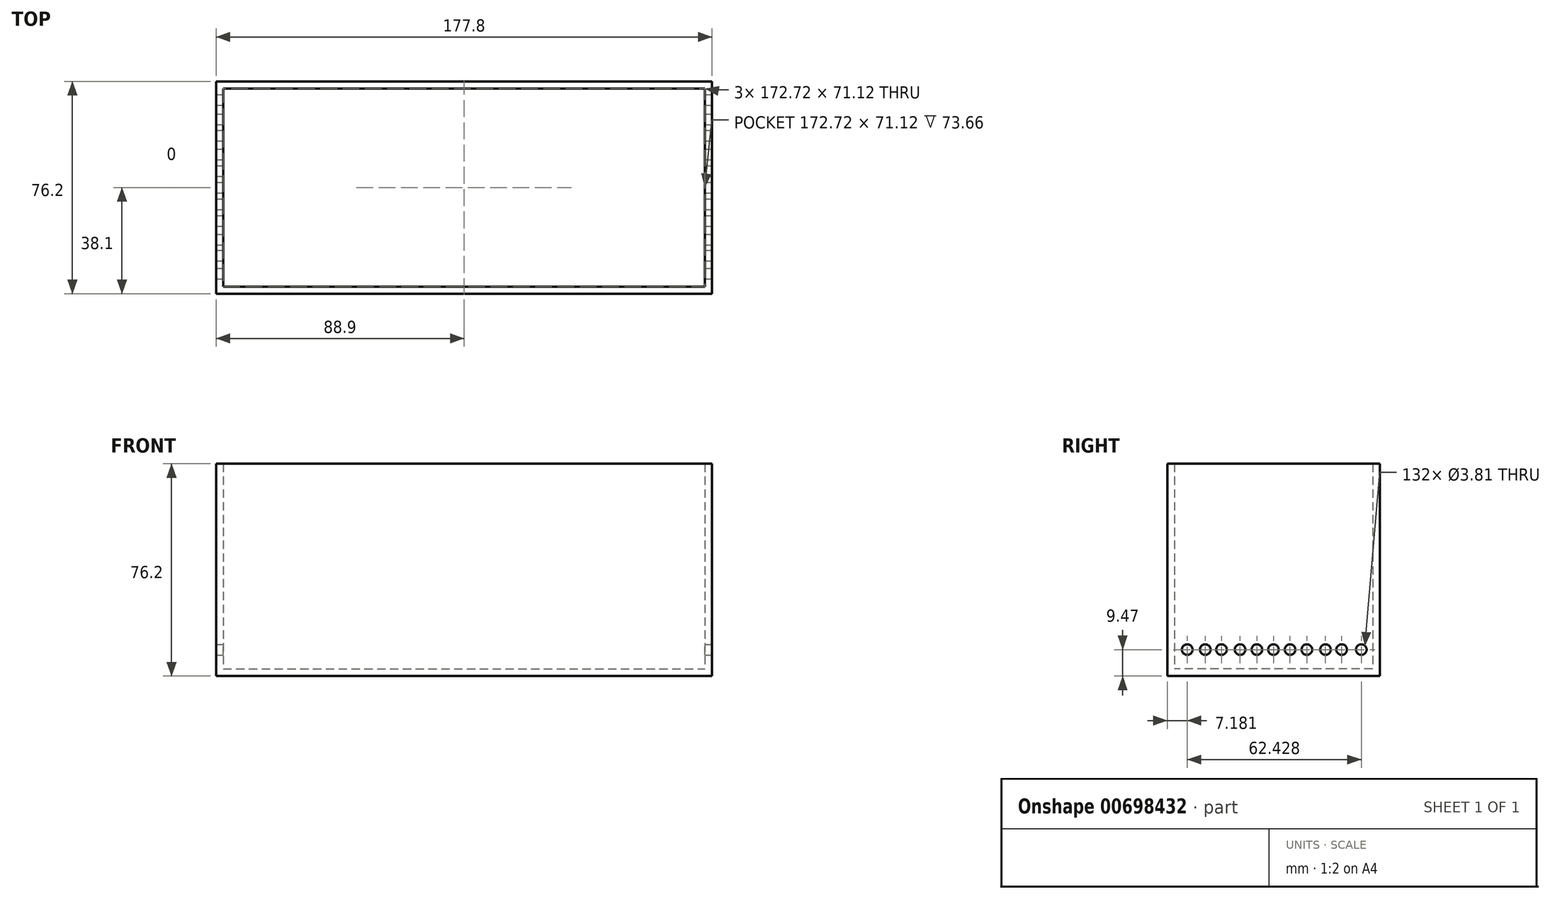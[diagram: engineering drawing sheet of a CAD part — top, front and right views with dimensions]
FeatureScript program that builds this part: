
annotation { "Feature Type Name" : "Feature", "Feature Type Description" : "" }
export const myFeature = defineFeature(function(context is Context, id is Id, definition is map)
    precondition{}
    {
        {
            var Q0;
            Q0=qCreatedBy(makeId("Top.planeOp"),FACE);
            var sketch = newSketch(context, id + "F0", { "sketchPlane" : qUnion([Q0])});
            skLineSegment(sketch, "E0.bottom", {"start": v(-88.9, 38.1) * mm, "end": v(88.9, 38.1) * mm});
            skLineSegment(sketch, "E0.top", {"start": v(-88.9, -38.1) * mm, "end": v(88.9, -38.1) * mm});
            skLineSegment(sketch, "E0.left", {"start": v(-88.9, 38.1) * mm, "end": v(-88.9, -38.1) * mm});
            skLineSegment(sketch, "E0.right", {"start": v(88.9, 38.1) * mm, "end": v(88.9, -38.1) * mm});
            skPoint(sketch, "E0.middle", {"position": v(0, 0) * mm});
            skSolve(sketch);
        }
        {
            var Q0;
            Q0=makeQuery(id+"F0.imprint","IMPRINT",FACE,{"disambiguationData":[TD([[makeQuery(id+"F0.imprint","IMPRINT",EDGE,{"derivedFrom":sQuery(id+"F0.wireOp",EDGE,"E0.bottom")}),-1.0]])]});
            extrude(context, id + "F1", {"entities" : qUnion([Q0]), "depth" : 76.2 * mm, "offsetDistance" : 25.4 * mm});
        }
        {
            var Q0;
            Q0=makeQuery(id+"F1.opExtrude","SWEPT_FACE",FACE,{"disambiguationData":[OSD([sQuery(id+"F0.wireOp",EDGE,"E0.right")])]});
            var sketch = newSketch(context, id + "F2", { "sketchPlane" : qUnion([Q0])});
            skPoint(sketch, "E1", {"position": v(0, 9.47) * mm});
            skPoint(sketch, "E2", {"position": v(-5.95, 9.47) * mm});
            skPoint(sketch, "E3", {"position": v(-11.97, 9.47) * mm});
            skPoint(sketch, "E4", {"position": v(-18.65, 9.47) * mm});
            skPoint(sketch, "E5", {"position": v(-24.46, 9.47) * mm});
            skPoint(sketch, "E6", {"position": v(-30.92, 9.47) * mm});
            skPoint(sketch, "E7.MirrorP", {"position": v(24.46, 9.47) * mm});
            skPoint(sketch, "E8.MirrorP", {"position": v(18.65, 9.47) * mm});
            skPoint(sketch, "E9.MirrorP", {"position": v(5.95, 9.47) * mm});
            skPoint(sketch, "E10.MirrorP", {"position": v(11.97, 9.47) * mm});
            skPoint(sketch, "E11", {"position": v(31.5, 9.47) * mm});
            skSolve(sketch);
        }
        {
            var Q0;
            Q0=makeQuery(id+"F1.opExtrude","CAP_FACE",FACE,{"disambiguationData":[OSD([sQuery(id+"F0.wireOp",EDGE,"E0.bottom"),sQuery(id+"F0.wireOp",EDGE,"E0.top"),sQuery(id+"F0.wireOp",EDGE,"E0.left"),sQuery(id+"F0.wireOp",EDGE,"E0.right")])],"isStart":false});
            shell(context, id + "F3", {"entities" : qUnion([Q0]), "thickness" : 2.54 * mm});
        }
        {
            var Q0;
            Q0=sQuery(id+"F2.wireOp",VERTEX,"E6");
            var Q1;
            Q1=sQuery(id+"F2.wireOp",VERTEX,"E5");
            var Q2;
            Q2=sQuery(id+"F2.wireOp",VERTEX,"E4");
            var Q3;
            Q3=sQuery(id+"F2.wireOp",VERTEX,"E2");
            var Q4;
            Q4=sQuery(id+"F2.wireOp",VERTEX,"E3");
            var Q5;
            Q5=sQuery(id+"F2.wireOp",VERTEX,"E1");
            var Q6;
            Q6=sQuery(id+"F2.wireOp",VERTEX,"E9.MirrorP");
            var Q7;
            Q7=sQuery(id+"F2.wireOp",VERTEX,"E10.MirrorP");
            var Q8;
            Q8=sQuery(id+"F2.wireOp",VERTEX,"E8.MirrorP");
            var Q9;
            Q9=sQuery(id+"F2.wireOp",VERTEX,"E7.MirrorP");
            var Q10;
            Q10=sQuery(id+"F2.wireOp",VERTEX,"E11");
            var Q11;
            Q11=makeQuery(id+"F1.opExtrude","SWEPT_BODY",BODY,{"disambiguationData":[OSD([sQuery(id+"F0.wireOp",EDGE,"E0.bottom"),sQuery(id+"F0.wireOp",EDGE,"E0.top"),sQuery(id+"F0.wireOp",EDGE,"E0.left"),sQuery(id+"F0.wireOp",EDGE,"E0.right")])]});
            hole(context, id + "F4", {"style" : HoleStyle.SIMPLE, "endStyle" : HoleEndStyle.THROUGH, "holeDiameter" : 3.8 * mm, "majorDiameter" : 6.35 * mm, "isTappedThrough" : true, "tappedDepth" : 12.7 * mm, "tapClearance" : 3, "locations" : qUnion([Q0, Q1, Q2, Q3, Q4, Q5, Q6, Q7, Q8, Q9, Q10]), "scope" : qUnion([Q11])});
        }
    });
